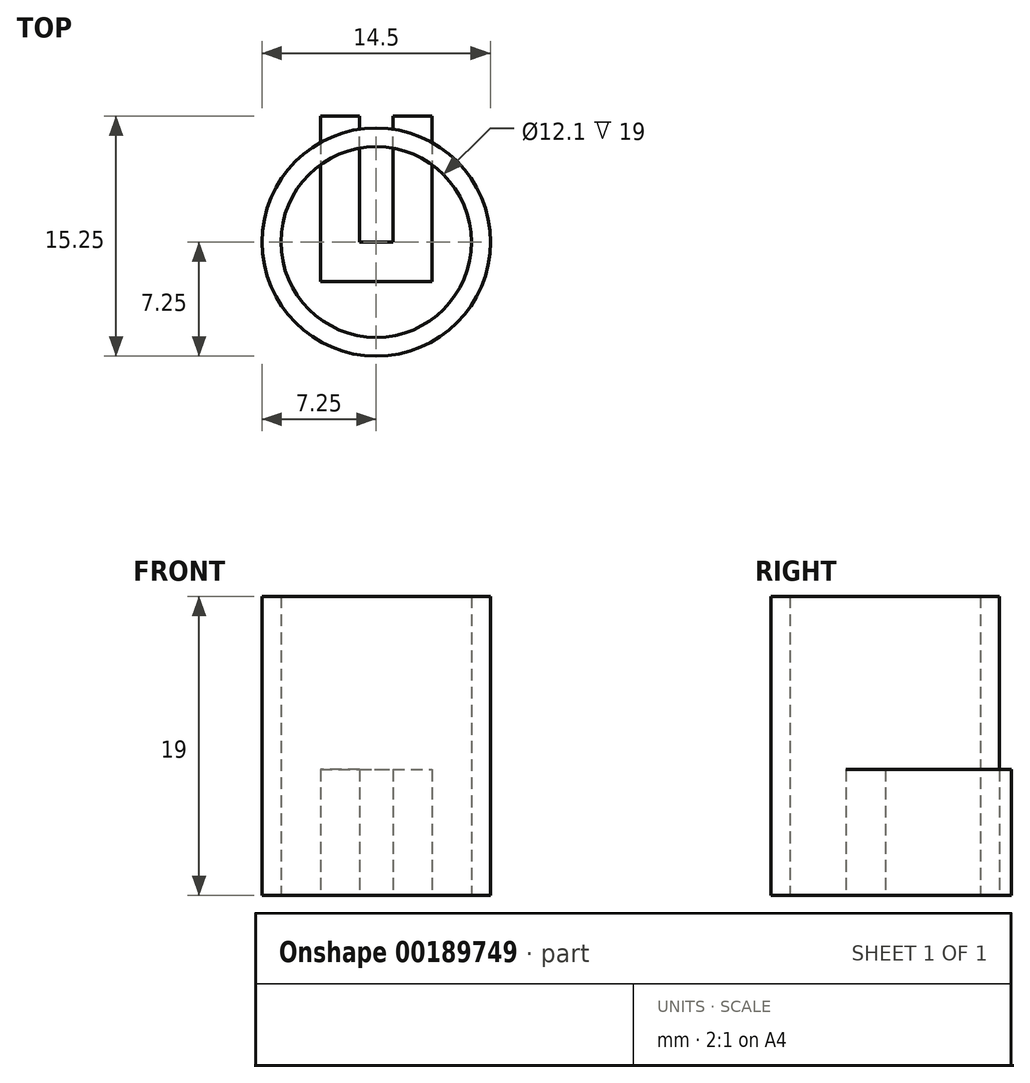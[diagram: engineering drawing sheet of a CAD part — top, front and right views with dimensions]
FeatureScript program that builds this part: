
annotation { "Feature Type Name" : "Feature", "Feature Type Description" : "" }
export const myFeature = defineFeature(function(context is Context, id is Id, definition is map)
    precondition{}
    {
        {
            var Q0;
            Q0=qCreatedBy(makeId("Top.planeOp"),FACE);
            var sketch = newSketch(context, id + "F0", { "sketchPlane" : qUnion([Q0])});
            skLineSegment(sketch, "E0", {"start": v(0, 0) * mm, "end": v(1.05, 0) * mm});
            skLineSegment(sketch, "E1", {"start": v(1.05, 0) * mm, "end": v(1.05, 8) * mm});
            skLineSegment(sketch, "E2", {"start": v(1.05, 8) * mm, "end": v(3.55, 8) * mm});
            skLineSegment(sketch, "E3", {"start": v(3.55, 8) * mm, "end": v(3.55, -2.5) * mm});
            skLineSegment(sketch, "E4", {"start": v(3.55, -2.5) * mm, "end": v(0, -2.5) * mm});
            skLineSegment(sketch, "E5.MirrorCS", {"start": v(0, 0) * mm, "end": v(-1.05, 0) * mm});
            skLineSegment(sketch, "E6.MirrorCS", {"start": v(-1.05, 8) * mm, "end": v(-3.55, 8) * mm});
            skLineSegment(sketch, "E7.MirrorCS", {"start": v(-3.55, -2.5) * mm, "end": v(0, -2.5) * mm});
            skLineSegment(sketch, "E8.MirrorCS", {"start": v(-3.55, 8) * mm, "end": v(-3.55, -2.5) * mm});
            skLineSegment(sketch, "E9.MirrorCS", {"start": v(-1.05, 0) * mm, "end": v(-1.05, 8) * mm});
            skSolve(sketch);
        }
        {
            var Q0;
            Q0=makeQuery(id+"F0.imprint","IMPRINT",FACE,{"disambiguationData":[TD([[makeQuery(id+"F0.imprint","IMPRINT",EDGE,{"derivedFrom":sQuery(id+"F0.wireOp",EDGE,"E0")}),-1.0]])]});
            extrude(context, id + "F1", {"entities" : qUnion([Q0]), "depth" : 8 * mm});
        }
        {
            var Q0;
            Q0=qCreatedBy(makeId("Top.planeOp"),FACE);
            var sketch = newSketch(context, id + "F2", { "sketchPlane" : qUnion([Q0])});
            skCircle(sketch, "E10", {"center": v(0, 0) * mm, "radius": 6.05 * mm});
            skCircle(sketch, "E11.0", {"center": v(0, 0) * mm, "radius": 7.25 * mm});
            skSolve(sketch);
        }
        {
            var Q0;
            Q0=makeQuery(id+"F2.imprint","IMPRINT",FACE,{"disambiguationData":[TD([[makeQuery(id+"F2.imprint","IMPRINT",EDGE,{"derivedFrom":sQuery(id+"F2.wireOp",EDGE,"E10")}),-1.0]])]});
            extrude(context, id + "F3", {"entities" : qUnion([Q0]), "depth" : 19 * mm});
        }
    });
